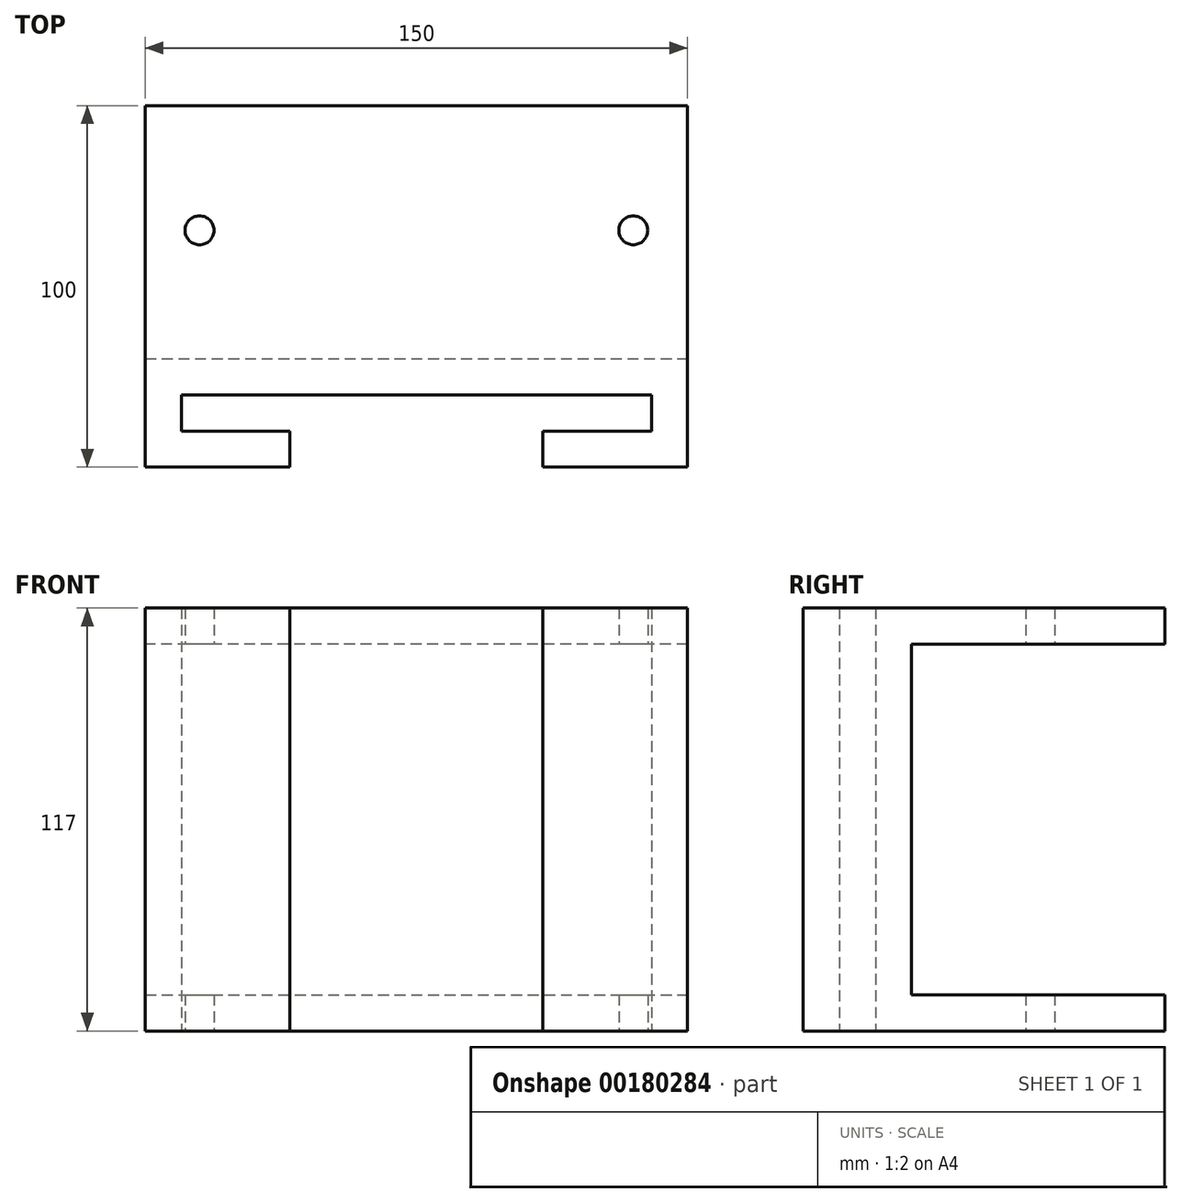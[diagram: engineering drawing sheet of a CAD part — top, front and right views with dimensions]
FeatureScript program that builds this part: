
annotation { "Feature Type Name" : "Feature", "Feature Type Description" : "" }
export const myFeature = defineFeature(function(context is Context, id is Id, definition is map)
    precondition{}
    {
        {
            var Q0;
            Q0=qCreatedBy(makeId("Top.planeOp"),FACE);
            var sketch = newSketch(context, id + "F0", { "sketchPlane" : qUnion([Q0])});
            skLineSegment(sketch, "E0", {"start": v(-35, -30) * mm, "end": v(-75, -30) * mm});
            skLineSegment(sketch, "E1", {"start": v(-75, -30) * mm, "end": v(-75, 0) * mm});
            skLineSegment(sketch, "E2", {"start": v(-75, 0) * mm, "end": v(75, 0) * mm});
            skLineSegment(sketch, "E3", {"start": v(75, 0) * mm, "end": v(75, -30) * mm});
            skLineSegment(sketch, "E4", {"start": v(75, -30) * mm, "end": v(35, -30) * mm});
            skLineSegment(sketch, "E5", {"start": v(35, -30) * mm, "end": v(35, -20) * mm});
            skLineSegment(sketch, "E6", {"start": v(35, -20) * mm, "end": v(65, -20) * mm});
            skLineSegment(sketch, "E7", {"start": v(65, -20) * mm, "end": v(65, -10) * mm});
            skLineSegment(sketch, "E8", {"start": v(65, -10) * mm, "end": v(-65, -10) * mm});
            skLineSegment(sketch, "E9", {"start": v(-65, -10) * mm, "end": v(-65, -20) * mm});
            skLineSegment(sketch, "E10", {"start": v(-65, -20) * mm, "end": v(-35, -20) * mm});
            skLineSegment(sketch, "E11", {"start": v(-35, -20) * mm, "end": v(-35, -30) * mm});
            skSolve(sketch);
        }
        {
            var Q0;
            Q0 = qSketchRegion(id + "F0", true);
            extrude(context, id + "F1", {"entities" : qUnion([Q0]), "depth" : 117 * mm});
        }
        {
            var Q0;
            Q0=makeQuery(id+"F1.opExtrude","SWEPT_FACE",FACE,{"disambiguationData":[OSD([sQuery(id+"F0.wireOp",EDGE,"E2")])]});
            var sketch = newSketch(context, id + "F2", { "sketchPlane" : qUnion([Q0])});
            skLineSegment(sketch, "E12.bottom", {"start": v(-75, 117) * mm, "end": v(75, 117) * mm});
            skLineSegment(sketch, "E12.top", {"start": v(-75, 107) * mm, "end": v(75, 107) * mm});
            skLineSegment(sketch, "E12.left", {"start": v(-75, 117) * mm, "end": v(-75, 107) * mm});
            skLineSegment(sketch, "E12.right", {"start": v(75, 117) * mm, "end": v(75, 107) * mm});
            skLineSegment(sketch, "E13.bottom", {"start": v(75, 0) * mm, "end": v(-75, 0) * mm});
            skLineSegment(sketch, "E13.top", {"start": v(75, 10) * mm, "end": v(-75, 10) * mm});
            skLineSegment(sketch, "E13.left", {"start": v(75, 0) * mm, "end": v(75, 10) * mm});
            skLineSegment(sketch, "E13.right", {"start": v(-75, 0) * mm, "end": v(-75, 10) * mm});
            skSolve(sketch);
        }
        {
            var Q0;
            Q0=makeQuery(id+"F2.imprint","IMPRINT",FACE,{"disambiguationData":[TD([[makeQuery(id+"F2.imprint","IMPRINT",EDGE,{"derivedFrom":sQuery(id+"F2.wireOp",EDGE,"E12.bottom")}),1.0]])]});
            var Q1;
            Q1=makeQuery(id+"F2.imprint","IMPRINT",FACE,{"disambiguationData":[TD([[makeQuery(id+"F2.imprint","IMPRINT",EDGE,{"derivedFrom":sQuery(id+"F2.wireOp",EDGE,"E13.bottom")}),-1.0]])]});
            extrude(context, id + "F3", {"entities" : qUnion([Q0, Q1]), "operationType" : NewBodyOperationType.ADD, "depth" : 70 * mm});
        }
        {
            var Q0;
            Q0=makeQuery(id+"F3.boolean.opBoolean","MERGE",FACE,{"derivedFrom":[makeQuery(id+"F1.opExtrude","CAP_FACE",FACE,{"disambiguationData":[OSD([sQuery(id+"F0.wireOp",EDGE,"E0"),sQuery(id+"F0.wireOp",EDGE,"E1"),sQuery(id+"F0.wireOp",EDGE,"E2"),sQuery(id+"F0.wireOp",EDGE,"E3"),sQuery(id+"F0.wireOp",EDGE,"E4"),sQuery(id+"F0.wireOp",EDGE,"E5"),sQuery(id+"F0.wireOp",EDGE,"E6"),sQuery(id+"F0.wireOp",EDGE,"E7"),sQuery(id+"F0.wireOp",EDGE,"E8"),sQuery(id+"F0.wireOp",EDGE,"E9"),sQuery(id+"F0.wireOp",EDGE,"E10"),sQuery(id+"F0.wireOp",EDGE,"E11")])],"isStart":true}),makeQuery(id+"F3.opExtrude","SWEPT_FACE",FACE,{"disambiguationData":[OSD([sQuery(id+"F2.wireOp",EDGE,"E13.bottom")])]})]});
            var sketch = newSketch(context, id + "F4", { "sketchPlane" : qUnion([Q0])});
            skCircle(sketch, "E14", {"center": v(-60, -35.5) * mm, "radius": 4 * mm});
            skCircle(sketch, "E15.MirrorC", {"center": v(60, -35.5) * mm, "radius": 4 * mm});
            skSolve(sketch);
        }
        {
            var Q0;
            Q0 = qSketchRegion(id + "F4", true);
            extrude(context, id + "F5", {"entities" : qUnion([Q0]), "operationType" : NewBodyOperationType.REMOVE, "oppositeDirection" : true, "depth" : 139.1 * mm});
        }
    });
